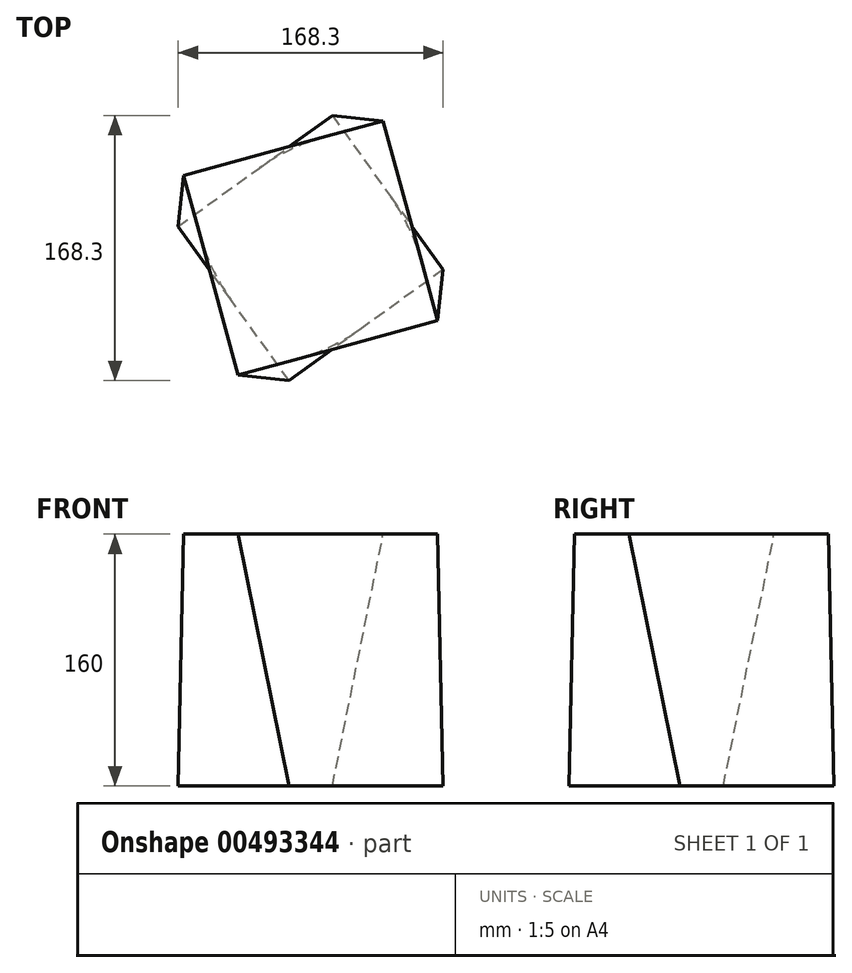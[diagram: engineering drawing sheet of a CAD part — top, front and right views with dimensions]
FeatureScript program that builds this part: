
annotation { "Feature Type Name" : "Feature", "Feature Type Description" : "" }
export const myFeature = defineFeature(function(context is Context, id is Id, definition is map)
    precondition{}
    {
        {
            var Q0;
            Q0=qCreatedBy(makeId("Top.planeOp"),FACE);
            var sketch = newSketch(context, id + "F0", { "sketchPlane" : qUnion([Q0])});
            skCircle(sketch, "E0.cCircle", {"center": v(0, 0) * mm, "radius": 85.27 * mm, "construction": true});
            skLineSegment(sketch, "E0.0", {"start": v(-84.15, 13.8) * mm, "end": v(13.8, 84.15) * mm});
            skLineSegment(sketch, "E0.1", {"start": v(13.8, 84.15) * mm, "end": v(84.15, -13.8) * mm});
            skLineSegment(sketch, "E0.2", {"start": v(84.15, -13.8) * mm, "end": v(-13.8, -84.15) * mm});
            skLineSegment(sketch, "E0.3", {"start": v(-13.8, -84.15) * mm, "end": v(-84.15, 13.8) * mm});
            skSolve(sketch);
        }
        {
            var Q0;
            Q0=qCreatedBy(makeId("Top.planeOp"),FACE);
            cPlane(context, id + "F1", {"entities" : qUnion([Q0]), "cplaneType" : CPlaneType.OFFSET, "offset" : 160 * mm, "width" : 150 * mm, "height" : 150 * mm});
        }
        {
            var Q0;
            Q0=qCreatedBy(id+"F1.planeOp",FACE);
            var sketch = newSketch(context, id + "F2", { "sketchPlane" : qUnion([Q0])});
            skCircle(sketch, "E1.cCircle", {"center": v(0, 0) * mm, "radius": 92.95 * mm, "construction": true});
            skLineSegment(sketch, "E1.0", {"start": v(-46.12, -80.7) * mm, "end": v(-80.7, 46.12) * mm});
            skLineSegment(sketch, "E1.1", {"start": v(-80.7, 46.12) * mm, "end": v(46.12, 80.7) * mm});
            skLineSegment(sketch, "E1.2", {"start": v(46.12, 80.7) * mm, "end": v(80.7, -46.12) * mm});
            skLineSegment(sketch, "E1.3", {"start": v(80.7, -46.12) * mm, "end": v(-46.12, -80.7) * mm});
            skSolve(sketch);
        }
        {
            var Q0;
            Q0=makeQuery(id+"F0.imprint","IMPRINT",FACE,{"disambiguationData":[TD([[makeQuery(id+"F0.imprint","IMPRINT",EDGE,{"derivedFrom":sQuery(id+"F0.wireOp",EDGE,"E0.0")}),-1.0]])]});
            var Q1;
            Q1=makeQuery(id+"F2.imprint","IMPRINT",FACE,{"disambiguationData":[TD([[makeQuery(id+"F2.imprint","IMPRINT",EDGE,{"derivedFrom":sQuery(id+"F2.wireOp",EDGE,"E1.0")}),-1.0]])]});
            loft(context, id + "F3", {"sheetProfilesArray" : [{ "sheetProfileEntities" : qUnion([Q0]) }, { "sheetProfileEntities" : qUnion([Q1]) }]});
        }
    });
